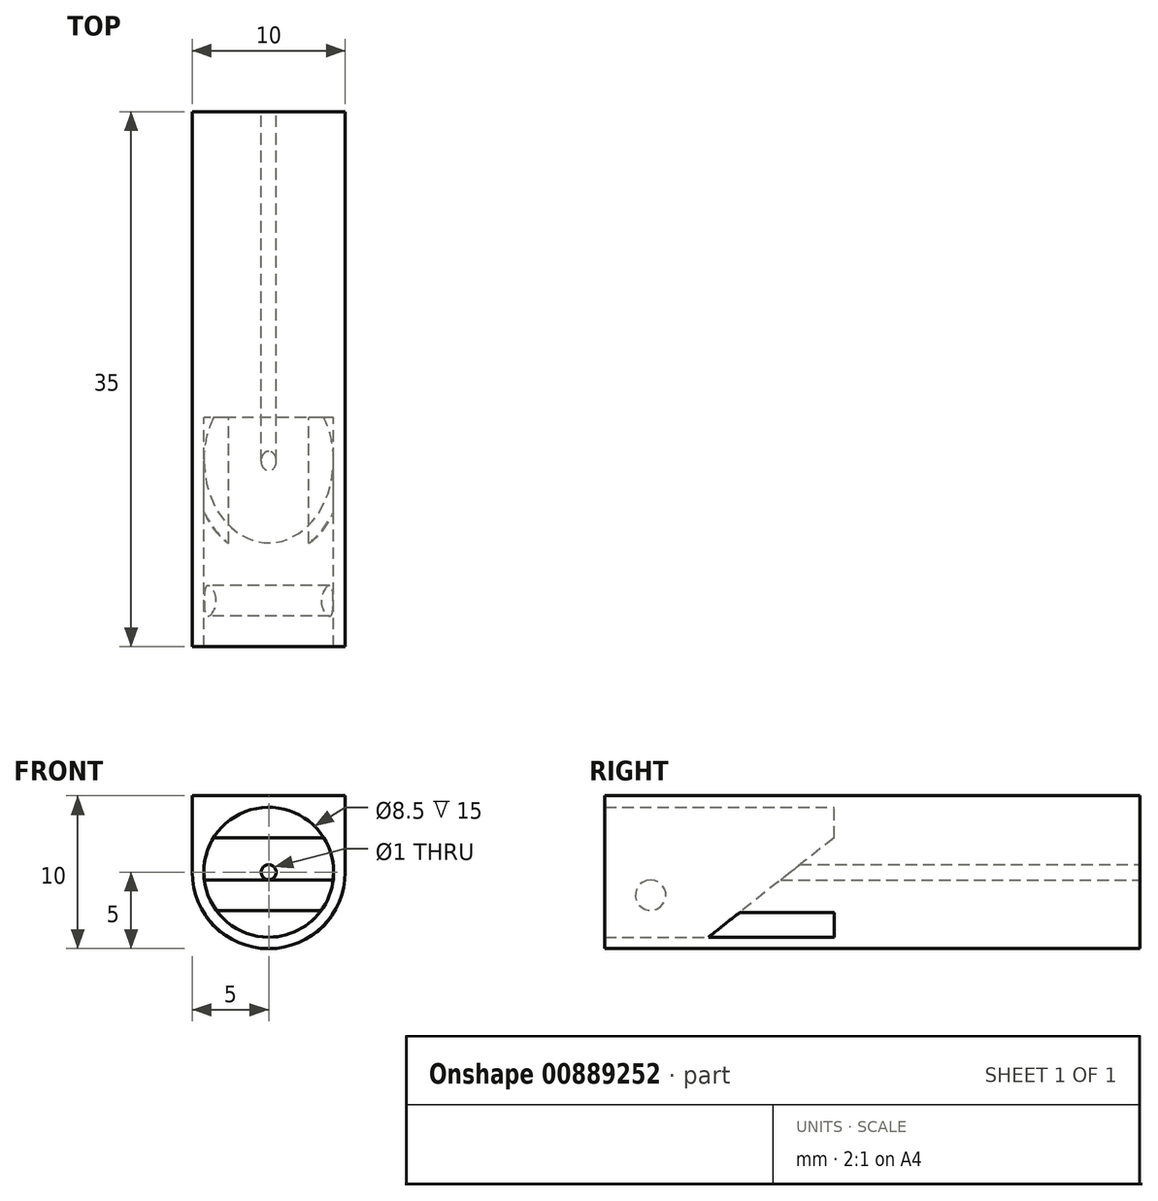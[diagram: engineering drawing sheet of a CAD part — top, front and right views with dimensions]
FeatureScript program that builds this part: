
annotation { "Feature Type Name" : "Feature", "Feature Type Description" : "" }
export const myFeature = defineFeature(function(context is Context, id is Id, definition is map)
    precondition{}
    {
        {
            var Q0;
            Q0=qCreatedBy(makeId("Front.planeOp"),FACE);
            var sketch = newSketch(context, id + "F0", { "sketchPlane" : qUnion([Q0])});
            skCircle(sketch, "E0", {"center": v(0, 5) * mm, "radius": 5 * mm});
            skCircle(sketch, "E1", {"center": v(0, 5) * mm, "radius": 4.25 * mm});
            skCircle(sketch, "E2", {"center": v(0, 5) * mm, "radius": 0.5 * mm});
            skLineSegment(sketch, "E3", {"start": v(5, 5) * mm, "end": v(5, 10) * mm});
            skLineSegment(sketch, "E4", {"start": v(5, 10) * mm, "end": v(0, 10) * mm});
            skLineSegment(sketch, "E5", {"start": v(0, 10) * mm, "end": v(-5, 10) * mm});
            skLineSegment(sketch, "E6", {"start": v(-5, 10) * mm, "end": v(-5, 5) * mm});
            skSolve(sketch);
        }
        {
            var Q0;
            Q0=qCreatedBy(makeId("Right.planeOp"),FACE);
            var sketch = newSketch(context, id + "F1", { "sketchPlane" : qUnion([Q0])});
            skCircle(sketch, "E7", {"center": v(-32, 3.5) * mm, "radius": 1 * mm});
            skLineSegment(sketch, "E8", {"start": v(-20, 0.75) * mm, "end": v(-28.22, 0.75) * mm});
            skLineSegment(sketch, "E9", {"start": v(-28.22, 0.75) * mm, "end": v(-20, 7.25) * mm});
            skLineSegment(sketch, "E10", {"start": v(-20, 7.25) * mm, "end": v(-20, 0.75) * mm});
            skSolve(sketch);
        }
        {
            var Q0;
            Q0=makeQuery(id+"F1.imprint","IMPRINT",FACE,{"disambiguationData":[TD([[makeQuery(id+"F1.imprint","IMPRINT",EDGE,{"derivedFrom":sQuery(id+"F1.wireOp",EDGE,"E7")}),1.0]])]});
            var Q1;
            Q1=makeQuery(id+"F1.imprint","IMPRINT",FACE,{"disambiguationData":[TD([[makeQuery(id+"F1.imprint","IMPRINT",EDGE,{"derivedFrom":sQuery(id+"F1.wireOp",EDGE,"E8")}),-1.0]])]});
            extrude(context, id + "F2", {"entities" : qUnion([Q0, Q1]), "endBound" : BoundingType.SYMMETRIC, "depth" : 8.5 * mm, "offsetDistance" : 25 * mm});
        }
        {
            var Q0;
            Q0=makeQuery(id+"F0.imprint","IMPRINT",FACE,{"disambiguationData":[TD([[makeQuery(id+"F0.imprint","IMPRINT",EDGE,{"derivedFrom":sQuery(id+"F0.wireOp",EDGE,"E1")}),1.0]])]});
            extrude(context, id + "F3", {"entities" : qUnion([Q0]), "depth" : 20 * mm, "offsetDistance" : 25 * mm});
        }
        {
            var Q0;
            Q0 = qSketchRegion(id + "F0", true);
            extrude(context, id + "F4", {"entities" : qUnion([Q0]), "operationType" : NewBodyOperationType.ADD, "depth" : 35 * mm, "offsetDistance" : 25 * mm});
        }
        {
            var Q0;
            Q0=makeQuery(id+"F0.imprint","IMPRINT",FACE,{"disambiguationData":[TD([[makeQuery(id+"F0.imprint","IMPRINT",EDGE,{"derivedFrom":sQuery(id+"F0.wireOp",EDGE,"E2")}),1.0]])]});
            extrude(context, id + "F5", {"entities" : qUnion([Q0]), "operationType" : NewBodyOperationType.REMOVE, "surfaceOperationType" : NewSurfaceOperationType.ADD, "oppositeDirection" : true, "depth" : -25 * mm, "offsetDistance" : 25 * mm});
        }
        {
            var Q0;
            Q0=makeQuery(id+"F2.opExtrude","CAP_EDGE",EDGE,{"disambiguationData":[OSD([sQuery(id+"F1.wireOp",EDGE,"E8")])],"isStart":true});
            var Q1;
            Q1=makeQuery(id+"F2.opExtrude","CAP_EDGE",EDGE,{"disambiguationData":[OSD([sQuery(id+"F1.wireOp",EDGE,"E8")])],"isStart":false});
            fillet(context, id + "F6", {"entities" : qUnion([Q0, Q1]), "radius" : 4 * mm, "tangentPropagation" : true, "allowEdgeOverflow" : false});
        }
    });
